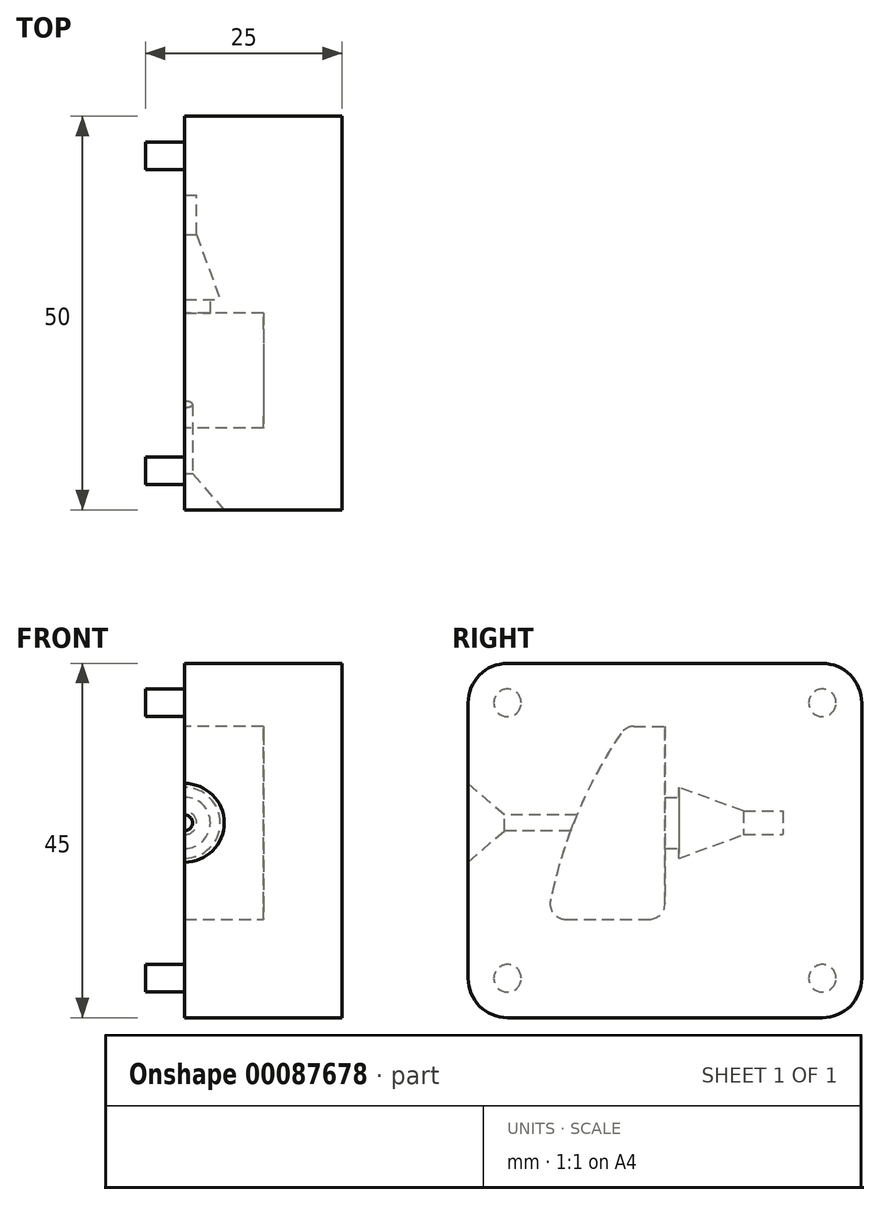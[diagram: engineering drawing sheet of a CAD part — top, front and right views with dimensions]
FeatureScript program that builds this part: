
annotation { "Feature Type Name" : "Feature", "Feature Type Description" : "" }
export const myFeature = defineFeature(function(context is Context, id is Id, definition is map)
    precondition{}
    {
        {
            var Q0;
            Q0=qCreatedBy(makeId("Right.planeOp"),FACE);
            var sketch = newSketch(context, id + "F0", { "sketchPlane" : qUnion([Q0])});
            skPoint(sketch, "E0.middle", {"position": v(0, 0) * mm});
            skLineSegment(sketch, "E1", {"start": v(0, 0) * mm, "end": v(-15, 0) * mm});
            skLineSegment(sketch, "E2", {"start": v(0, 0) * mm, "end": v(0, 24.5) * mm});
            skLineSegment(sketch, "E3", {"start": v(0, 24.5) * mm, "end": v(-5, 24.5) * mm});
            skArc(sketch, "E4", {"start": v(-5, 24.5) * mm, "mid": v(-11.37, 12.8) * mm, "end": v(-15, 0) * mm});
            skPoint(sketch, "E4.third.point", {"position": v(95.24, 21.65) * mm});
            skSolve(sketch);
        }
        {
            var Q0;
            Q0=qSketchRegion(id+"F0",true);
            extrude(context, id + "F1", {"entities" : qUnion([Q0]), "endBound" : BoundingType.SYMMETRIC, "depth" : 20 * mm});
        }
        {
            var Q0;
            Q0=makeQuery(id+"F1.opExtrude","SWEPT_FACE",FACE,{"disambiguationData":[OSD([sQuery(id+"F0.wireOp",EDGE,"E2")])]});
            var sketch = newSketch(context, id + "F2", { "sketchPlane" : qUnion([Q0])});
            skPoint(sketch, "E5", {"position": v(0, 12.25) * mm});
            skPoint(sketch, "E5.positionSnap0", {"position": v(-10, 12.25) * mm});
            skPoint(sketch, "E5.positionSnap1", {"position": v(0, 24.5) * mm});
            skSolve(sketch);
        }
        {
            var Q0;
            Q0=qCreatedBy(makeId("Right.planeOp"),FACE);
            var sketch = newSketch(context, id + "F3", { "sketchPlane" : qUnion([Q0])});
            skLineSegment(sketch, "E6", {"start": v(15, 12.25) * mm, "end": v(0, 12.25) * mm});
            skLineSegment(sketch, "E7", {"start": v(0, 15.5) * mm, "end": v(1.75, 15.5) * mm});
            skLineSegment(sketch, "E8", {"start": v(1.75, 15.5) * mm, "end": v(1.75, 16.75) * mm});
            skLineSegment(sketch, "E9", {"start": v(1.75, 16.75) * mm, "end": v(10, 13.75) * mm});
            skLineSegment(sketch, "E10", {"start": v(10, 13.75) * mm, "end": v(15, 13.75) * mm});
            skLineSegment(sketch, "E11", {"start": v(0, 15.5) * mm, "end": v(0, 12.25) * mm});
            skLineSegment(sketch, "E12", {"start": v(15, 13.75) * mm, "end": v(15, 12.25) * mm});
            skSolve(sketch);
        }
        {
            var Q0;
            Q0=makeQuery(id+"F3.imprint","IMPRINT",FACE,{"disambiguationData":[TD([[makeQuery(id+"F3.imprint","IMPRINT",EDGE,{"derivedFrom":sQuery(id+"F3.wireOp",EDGE,"E6")}),-1.0]])]});
            var Q1;
            Q1=sQuery(id+"F3.wireOp",EDGE,"E6");
            revolve(context, id + "F4", {"operationType" : NewBodyOperationType.ADD, "entities" : qUnion([Q0]), "axis" : qUnion([Q1]), "revolveType" : RevolveType.FULL});
        }
        {
            var Q0;
            Q0=makeQuery(id+"F1.opExtrude","SWEPT_EDGE",EDGE,{"disambiguationData":[OSD([sQuery(id+"F0.wireOp",EDGE,"E3"),sQuery(id+"F0.wireOp",EDGE,"E4")])]});
            var Q1;
            Q1=makeQuery(id+"F1.opExtrude","SWEPT_EDGE",EDGE,{"disambiguationData":[OSD([sQuery(id+"F0.wireOp",EDGE,"E1"),sQuery(id+"F0.wireOp",EDGE,"E4")])]});
            var Q2;
            Q2=makeQuery(id+"F1.opExtrude","SWEPT_EDGE",EDGE,{"disambiguationData":[OSD([sQuery(id+"F0.wireOp",EDGE,"E1"),sQuery(id+"F0.wireOp",EDGE,"E2")])]});
            fillet(context, id + "F5", {"entities" : qUnion([Q0, Q1, Q2]), "radius" : 2 * mm, "tangentPropagation" : true, "allowEdgeOverflow" : false});
        }
        {
            var Q0;
            Q0=qCreatedBy(makeId("Right.planeOp"),FACE);
            var sketch = newSketch(context, id + "F6", { "sketchPlane" : qUnion([Q0])});
            skLineSegment(sketch, "E13.top", {"start": v(25, 32.5) * mm, "end": v(-25, 32.5) * mm});
            skLineSegment(sketch, "E13.left", {"start": v(25, -12.5) * mm, "end": v(25, 32.5) * mm});
            skLineSegment(sketch, "E13.right", {"start": v(-25, -12.5) * mm, "end": v(-25, 32.5) * mm});
            skPoint(sketch, "E13.middle", {"position": v(0, 0) * mm});
            skLineSegment(sketch, "E14", {"start": v(-25, -12.5) * mm, "end": v(25, -12.5) * mm});
            skPoint(sketch, "E13.bottom.start.orphan", {"position": v(25, -32.5) * mm});
            skPoint(sketch, "E15.orphan", {"position": v(-25, -32.5) * mm});
            skSolve(sketch);
        }
        {
            var Q0;
            Q0 = qSketchRegion(id + "F6", true);
            extrude(context, id + "F7", {"entities" : qUnion([Q0]), "depth" : 20 * mm});
        }
        {
            var Q0;
            Q0=makeQuery(id+"F1.opExtrude","SWEPT_BODY",BODY,{"disambiguationData":[OSD([sQuery(id+"F0.wireOp",EDGE,"E1"),sQuery(id+"F0.wireOp",EDGE,"E2"),sQuery(id+"F0.wireOp",EDGE,"E3"),sQuery(id+"F0.wireOp",EDGE,"E4")])]});
            var Q1;
            Q1=makeQuery(id+"F7.opExtrude","SWEPT_BODY",BODY,{"disambiguationData":[OSD([sQuery(id+"F6.wireOp",EDGE,"E13.bottom"),sQuery(id+"F6.wireOp",EDGE,"E13.top"),sQuery(id+"F6.wireOp",EDGE,"E13.left"),sQuery(id+"F6.wireOp",EDGE,"E13.right")])]});
            booleanBodies(context, id + "F8", {"operationType" : BooleanOperationType.SUBTRACTION, "tools" : qUnion([Q0]), "targets" : qUnion([Q1])});
        }
        {
            var Q0;
            {var subQ0=makeQuery(id+"F7.opExtrude","SWEPT_FACE",FACE,{"disambiguationData":[OSD([sQuery(id+"F6.wireOp",EDGE,"E13.right")])]});Q0=makeQuery(id+"F3Q9CtZ0ULCDG1u_2.boolean.opBoolean","MERGE",FACE,{"derivedFrom":[subQ0,makeQuery(id+"F3Q9CtZ0ULCDG1u_2.opPattern","COPY",FACE,{"derivedFrom":subQ0,"instanceName":"1"})]});}
            var sketch = newSketch(context, id + "F9", { "sketchPlane" : qUnion([Q0])});
            skPoint(sketch, "E16", {"position": v(0, 12.25) * mm});
            skSolve(sketch);
        }
        {
            var Q0;
            Q0=sQuery(id+"F9.wireOp",VERTEX,"E16");
            var Q1;
            Q1=makeQuery(id+"F7.opExtrude","SWEPT_BODY",BODY,{"disambiguationData":[OSD([sQuery(id+"F6.wireOp",EDGE,"E13.top"),sQuery(id+"F6.wireOp",EDGE,"E13.left"),sQuery(id+"F6.wireOp",EDGE,"E13.right"),sQuery(id+"F6.wireOp",EDGE,"E14")])]});
            hole(context, id + "F10", {"style" : HoleStyle.C_SINK, "endStyle" : HoleEndStyle.BLIND, "holeDiameter" : 2 * mm, "cSinkDiameter" : 10 * mm, "cSinkAngle" : 82 * degree, "holeDepth" : 20 * mm, "locations" : qUnion([Q0]), "scope" : qUnion([Q1])});
        }
        {
            var Q0;
            Q0=makeQuery(id+"F7.opExtrude","SWEPT_EDGE",EDGE,{"disambiguationData":[OSD([sQuery(id+"F6.wireOp",EDGE,"E13.top"),sQuery(id+"F6.wireOp",EDGE,"E13.right")])]});
            var Q1;
            Q1=makeQuery(id+"F7.opExtrude","SWEPT_EDGE",EDGE,{"disambiguationData":[OSD([sQuery(id+"F6.wireOp",EDGE,"E13.top"),sQuery(id+"F6.wireOp",EDGE,"E13.left")])]});
            var Q2;
            Q2=makeQuery(id+"F7.opExtrude","SWEPT_EDGE",EDGE,{"disambiguationData":[OSD([sQuery(id+"F6.wireOp",EDGE,"E13.right"),sQuery(id+"F6.wireOp",EDGE,"E14")])]});
            var Q3;
            Q3=makeQuery(id+"F7.opExtrude","SWEPT_EDGE",EDGE,{"disambiguationData":[OSD([sQuery(id+"F6.wireOp",EDGE,"E13.left"),sQuery(id+"F6.wireOp",EDGE,"E14")])]});
            fillet(context, id + "F11", {"entities" : qUnion([Q0, Q1, Q2, Q3]), "radius" : 5 * mm, "tangentPropagation" : true, "allowEdgeOverflow" : false});
        }
        {
            var Q0;
            Q0=makeQuery(id+"F6.imprint","IMPRINT",FACE,{"disambiguationData":[TD([[makeQuery(id+"F6.imprint","IMPRINT",EDGE,{"derivedFrom":sQuery(id+"F6.wireOp",EDGE,"E13.top")}),1.0]])]});
            var sketch = newSketch(context, id + "F12", { "sketchPlane" : qUnion([Q0])});
            skLineSegment(sketch, "E17.bottom", {"start": v(-20, -7.5) * mm, "end": v(20, -7.5) * mm, "construction": true});
            skLineSegment(sketch, "E17.top", {"start": v(-20, 27.5) * mm, "end": v(20, 27.5) * mm, "construction": true});
            skLineSegment(sketch, "E17.left", {"start": v(-20, -7.5) * mm, "end": v(-20, 27.5) * mm, "construction": true});
            skLineSegment(sketch, "E17.right", {"start": v(20, -7.5) * mm, "end": v(20, 27.5) * mm, "construction": true});
            skPoint(sketch, "E17.middle", {"position": v(0, 10) * mm});
            skCircle(sketch, "E18", {"center": v(20, 27.5) * mm, "radius": 1.75 * mm});
            skCircle(sketch, "E19", {"center": v(-20, 27.5) * mm, "radius": 1.75 * mm});
            skCircle(sketch, "E20", {"center": v(-20, -7.5) * mm, "radius": 1.75 * mm});
            skCircle(sketch, "E21", {"center": v(20, -7.5) * mm, "radius": 1.75 * mm});
            skSolve(sketch);
        }
        {
            var Q0;
            Q0 = qSketchRegion(id + "F12", true);
            extrude(context, id + "F13", {"entities" : qUnion([Q0]), "operationType" : NewBodyOperationType.ADD, "oppositeDirection" : true, "depth" : 5 * mm});
        }
    });
